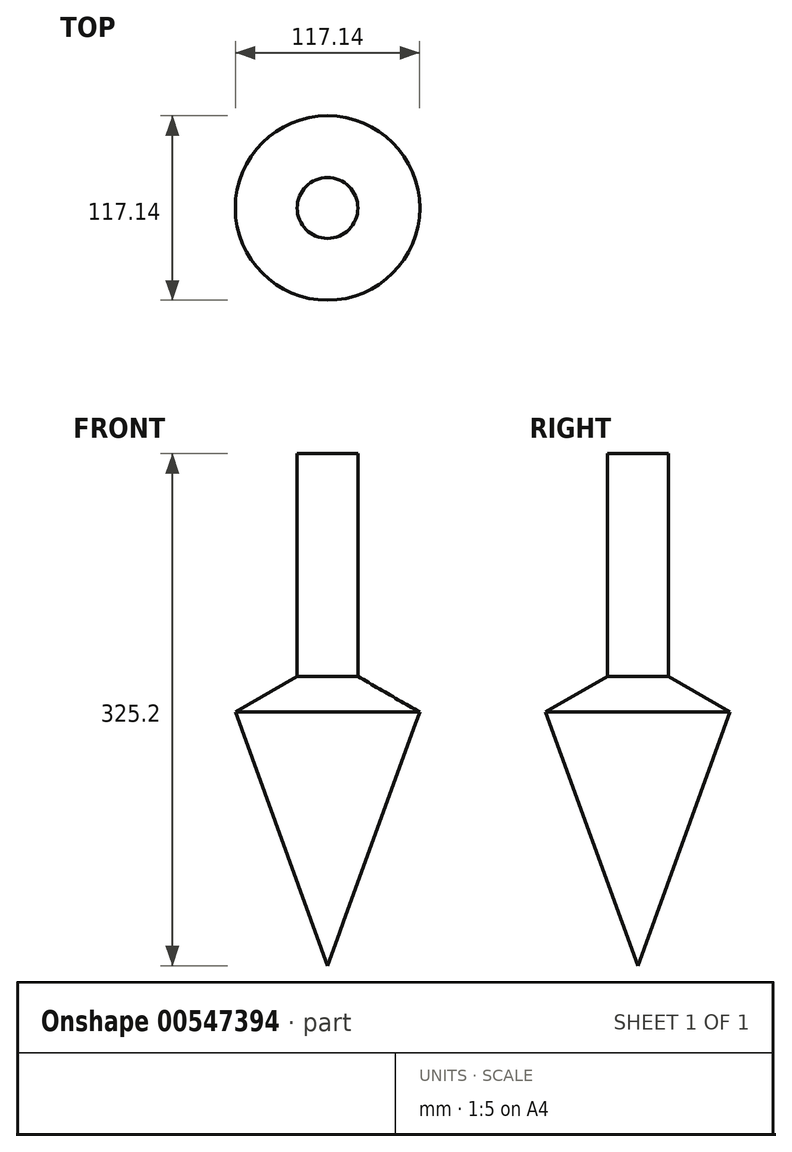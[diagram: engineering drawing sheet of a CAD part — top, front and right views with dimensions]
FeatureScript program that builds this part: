
annotation { "Feature Type Name" : "Feature", "Feature Type Description" : "" }
export const myFeature = defineFeature(function(context is Context, id is Id, definition is map)
    precondition{}
    {
        {
            var Q0;
            Q0=qCreatedBy(makeId("Front.planeOp"),FACE);
            var sketch = newSketch(context, id + "F0", { "sketchPlane" : qUnion([Q0])});
            skLineSegment(sketch, "E0", {"start": v(0, 0) * mm, "end": v(-19.3, 0) * mm});
            skLineSegment(sketch, "E1", {"start": v(-58.57, -22.68) * mm, "end": v(-19.3, 0) * mm});
            skLineSegment(sketch, "E2", {"start": v(-19.3, 0) * mm, "end": v(-19.3, 141.48) * mm});
            skLineSegment(sketch, "E3", {"start": v(-19.3, 141.48) * mm, "end": v(0, 141.48) * mm});
            skLineSegment(sketch, "E4", {"start": v(0, 141.48) * mm, "end": v(0, 0) * mm});
            skLineSegment(sketch, "E5", {"start": v(-58.57, -22.68) * mm, "end": v(0, -22.68) * mm});
            skLineSegment(sketch, "E6", {"start": v(0, -22.68) * mm, "end": v(0, 0) * mm});
            skLineSegment(sketch, "E7", {"start": v(0, -22.68) * mm, "end": v(0, -183.72) * mm});
            skLineSegment(sketch, "E8", {"start": v(-58.57, -22.68) * mm, "end": v(0, -183.72) * mm});
            skSolve(sketch);
        }
        {
            var Q0;
            Q0 = qSketchRegion(id + "F0", true);
            var Q1;
            Q1=sQuery(id+"F0.wireOp",EDGE,"E4");
            revolve(context, id + "F1", {"entities" : qUnion([Q0]), "axis" : qUnion([Q1]), "revolveType" : RevolveType.FULL});
        }
    });
